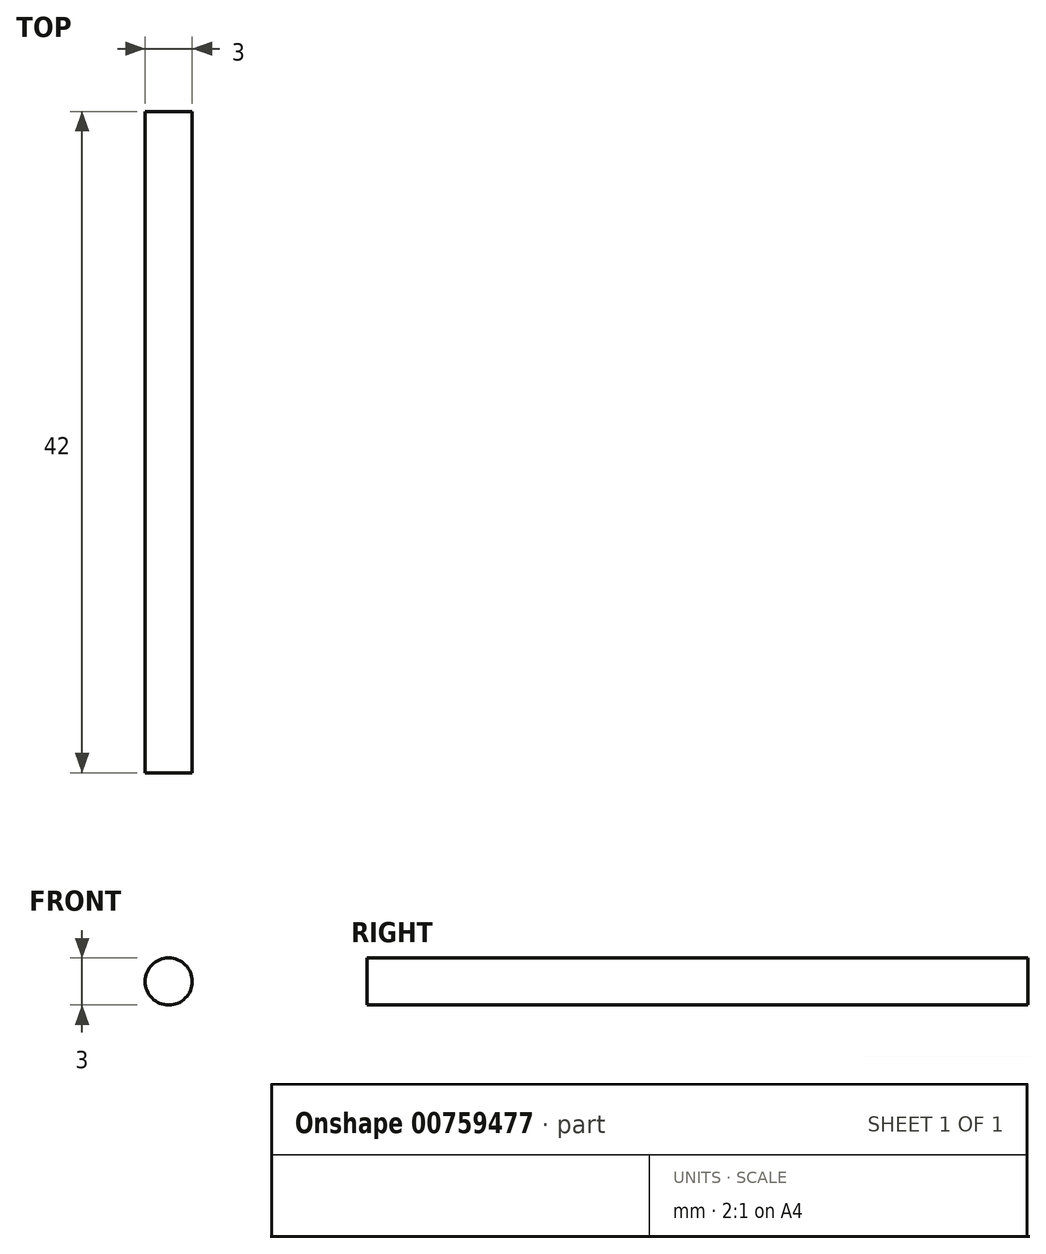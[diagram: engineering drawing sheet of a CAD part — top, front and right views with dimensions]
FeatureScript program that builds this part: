
annotation { "Feature Type Name" : "Feature", "Feature Type Description" : "" }
export const myFeature = defineFeature(function(context is Context, id is Id, definition is map)
    precondition{}
    {
        {
            var Q0;
            Q0=qCreatedBy(makeId("Front.planeOp"),FACE);
            var sketch = newSketch(context, id + "F0", { "sketchPlane" : qUnion([Q0])});
            skCircle(sketch, "E0", {"center": v(0, 0) * mm, "radius": 1.5 * mm});
            skSolve(sketch);
        }
        {
            var Q0;
            Q0 = qSketchRegion(id + "F0", true);
            extrude(context, id + "F1", {"entities" : qUnion([Q0]), "depth" : 42 * mm, "offsetDistance" : 25 * mm});
        }
    });
